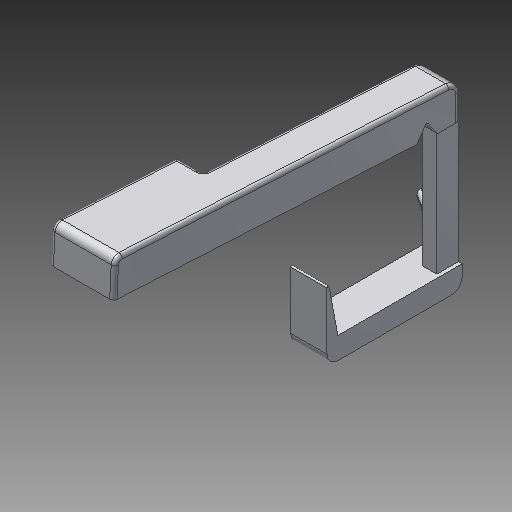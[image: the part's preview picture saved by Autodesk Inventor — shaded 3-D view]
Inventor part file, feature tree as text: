
AUTODESK INVENTOR PART (.ipt)
format: ipt  version: 2018 (Build 220112000, 112)  size: 320,512 bytes
history: native  units: mm
features: extrude x7, fillet x6, other x3, draft x1, chamfer x1
ambient origin geometry x8: Origin, YZ Plane, XZ Plane, XY Plane, X Axis, Y Axis, Z Axis, Center Point
bodies: Solid1 (feature_tree)
feature tree (18):
  other  "Key Sketch"
  extrude  "Upper Key"  Depth=10.0mm
  extrude  "Lower Key"  Depth=1.0mm
  other  "Hinge Cut Sketch"
  extrude  "Hinge Cut"  Depth=10.0mm TaperAngle=0.0deg
  extrude  "Hinge Cut 2"  Depth=3.0mm
  other  "Lever Sketch"
  extrude  "Vertical Lever"  Depth=3.0mm
  extrude  "Horizontal Lever"  Depth=33.6625mm
  extrude  "Spring Hook"  Depth=0.5mm
  draft  "FaceDraft3"
  chamfer  "Chamfer1"  Distance=3.0mm
  fillet  "Fillet9"  Radius=6.0mm
  fillet  "Fillet10"  Radius=4.0mm
  fillet  "Fillet5"  Radius=10.0mm
  fillet  "Fillet4"  [1 undecoded]
  fillet  "Fillet11"  Radius=3.0mm
  fillet  "Fillet14"  Radius=2.3mm
note: 1 required parameter value undecoded (feature->parameter linkage not recoverable at this tier; creation-order binding heuristic only, values carry confidence <= 0.55)
